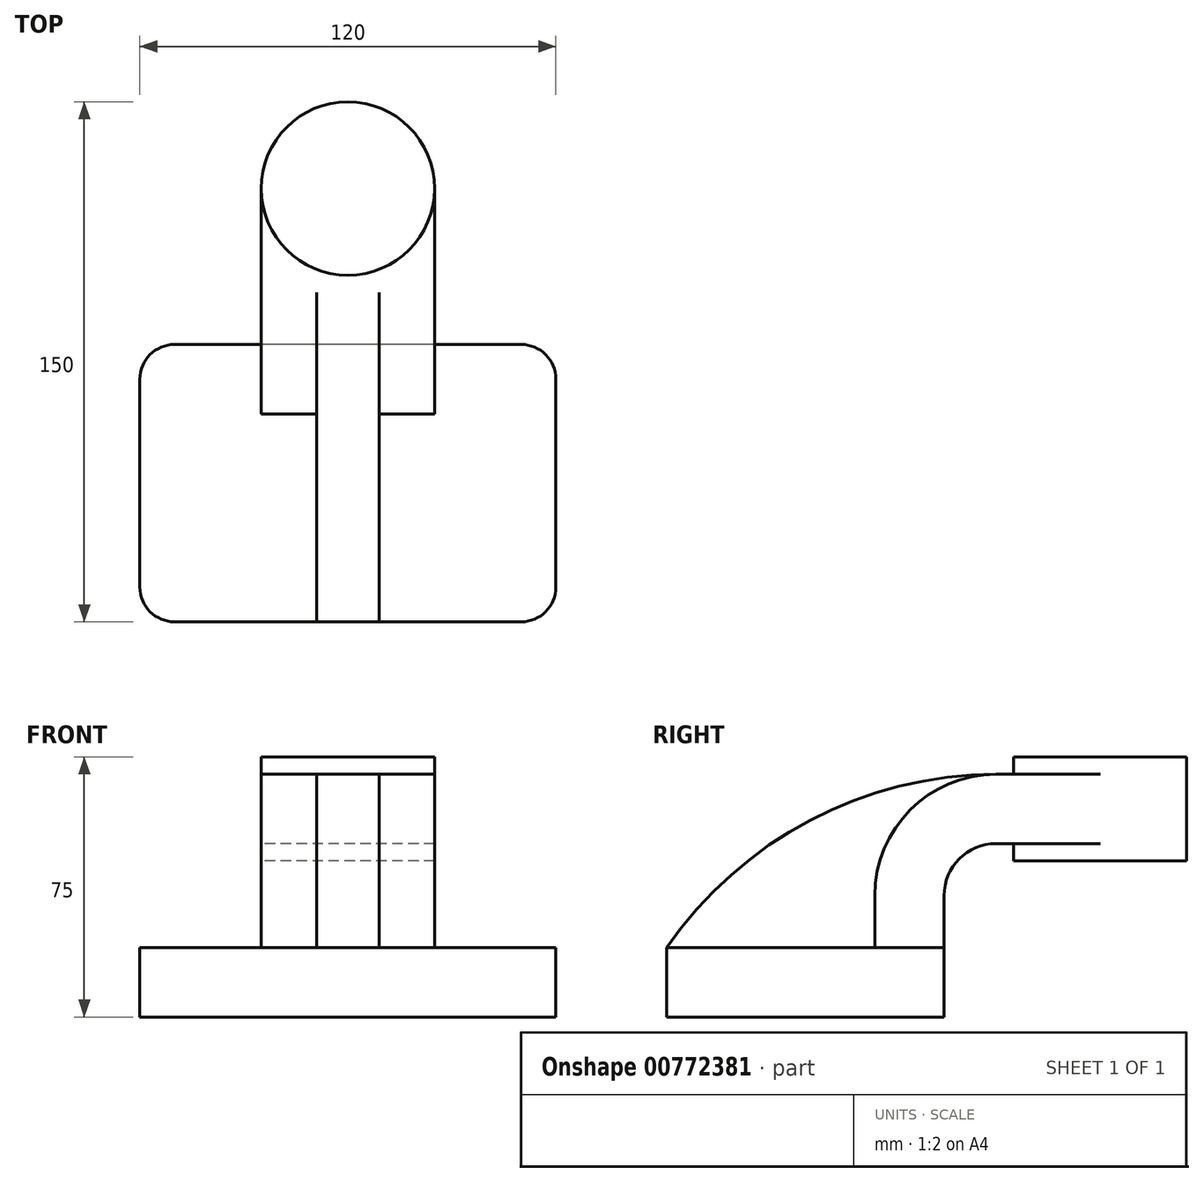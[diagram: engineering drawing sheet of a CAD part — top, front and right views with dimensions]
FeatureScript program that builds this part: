
annotation { "Feature Type Name" : "Feature", "Feature Type Description" : "" }
export const myFeature = defineFeature(function(context is Context, id is Id, definition is map)
    precondition{}
    {
        {
            var Q0;
            Q0=qCreatedBy(makeId("Right.planeOp"),FACE);
            var sketch = newSketch(context, id + "F0", { "sketchPlane" : qUnion([Q0])});
            skLineSegment(sketch, "E0", {"start": v(0, 0) * mm, "end": v(80, 0) * mm});
            skLineSegment(sketch, "E1", {"start": v(80, 0) * mm, "end": v(80, 20) * mm});
            skLineSegment(sketch, "E2", {"start": v(80, 20) * mm, "end": v(80, 35) * mm});
            skLineSegment(sketch, "E3", {"start": v(0, 0) * mm, "end": v(0, 20) * mm});
            skLineSegment(sketch, "E4", {"start": v(0, 20) * mm, "end": v(80, 20) * mm});
            skLineSegment(sketch, "E5", {"start": v(95, 70) * mm, "end": v(125, 70) * mm});
            skLineSegment(sketch, "E6", {"start": v(125, 70) * mm, "end": v(125, 50) * mm});
            skLineSegment(sketch, "E7", {"start": v(125, 50) * mm, "end": v(95, 50) * mm});
            skArc(sketch, "E8", {"start": v(80, 35) * mm, "mid": v(84.4, 45.6) * mm, "end": v(95, 50) * mm});
            skArc(sketch, "E9", {"start": v(95, 70) * mm, "mid": v(41.32, 56.74) * mm, "end": v(0, 20) * mm});
            skArc(sketch, "E10.0", {"start": v(60, 35) * mm, "mid": v(70.25, 59.75) * mm, "end": v(95, 70) * mm});
            skLineSegment(sketch, "E10.1", {"start": v(60, 20) * mm, "end": v(60, 35) * mm});
            skLineSegment(sketch, "E11.bottom", {"start": v(150, 45) * mm, "end": v(100, 45) * mm});
            skLineSegment(sketch, "E11.top", {"start": v(150, 75) * mm, "end": v(100, 75) * mm});
            skLineSegment(sketch, "E11.left", {"start": v(150, 45) * mm, "end": v(150, 75) * mm});
            skLineSegment(sketch, "E11.right", {"start": v(100, 45) * mm, "end": v(100, 75) * mm});
            skPoint(sketch, "E11.middle", {"position": v(125, 60) * mm});
            skLineSegment(sketch, "E12", {"start": v(125, 70) * mm, "end": v(125, 75) * mm});
            skLineSegment(sketch, "E13", {"start": v(125, 50) * mm, "end": v(125, 45) * mm});
            skSolve(sketch);
        }
        {
            var Q0;
            Q0=makeQuery(id+"F0.imprint","IMPRINT",FACE,{"disambiguationData":[TD([[makeQuery(id+"F0.imprint","IMPRINT",EDGE,{"derivedFrom":sQuery(id+"F0.wireOp",EDGE,"E0")}),1.0]])]});
            extrude(context, id + "F1", {"entities" : qUnion([Q0]), "endBound" : BoundingType.SYMMETRIC, "depth" : 120 * mm, "offsetDistance" : 25 * mm});
        }
        {
            var Q0;
            {var subQ0=sQuery(id+"F0.wireOp",EDGE,"E9");Q0=makeQuery(id+"F0.imprint","IMPRINT",FACE,{"disambiguationData":[TD([[makeQuery(id+"F0.imprint","IMPRINT",EDGE,{"derivedFrom":subQ0}),1.0]])]});}
            extrude(context, id + "F2", {"entities" : qUnion([Q0]), "operationType" : NewBodyOperationType.ADD, "endBound" : BoundingType.SYMMETRIC, "depth" : 18 * mm, "offsetDistance" : 25 * mm});
        }
        {
            var Q0;
            {var subQ8=sQuery(id+"F0.wireOp",EDGE,"E2");Q0=makeQuery(id+"F0.imprint","IMPRINT",FACE,{"disambiguationData":[TD([[makeQuery(id+"F0.imprint","IMPRINT",EDGE,{"derivedFrom":subQ8}),1.0]])]});}
            var Q1;
            {var subQ0=sQuery(id+"F0.wireOp",EDGE,"E6");Q1=makeQuery(id+"F0.imprint","IMPRINT",FACE,{"disambiguationData":[TD([[makeQuery(id+"F0.imprint","IMPRINT",EDGE,{"derivedFrom":subQ0}),-1.0]])]});}
            extrude(context, id + "F3", {"entities" : qUnion([Q0, Q1]), "operationType" : NewBodyOperationType.ADD, "endBound" : BoundingType.SYMMETRIC, "depth" : 50 * mm, "offsetDistance" : 25 * mm});
        }
        {
            var Q0;
            Q0=makeQuery(id+"F0.imprint","IMPRINT",FACE,{"disambiguationData":[TD([[makeQuery(id+"F0.imprint","IMPRINT",EDGE,{"derivedFrom":sQuery(id+"F0.wireOp",EDGE,"E6")}),1.0]])]});
            var Q1;
            Q1=sQuery(id+"F0.wireOp",EDGE,"E13");
            revolve(context, id + "F4", {"operationType" : NewBodyOperationType.ADD, "surfaceOperationType" : NewSurfaceOperationType.NEW, "entities" : qUnion([Q0]), "axis" : qUnion([Q1]), "revolveType" : RevolveType.FULL});
        }
        {
            var Q0;
            Q0=makeQuery(id+"F1.opExtrude","CAP_EDGE",EDGE,{"disambiguationData":[OSD([sQuery(id+"F0.wireOp",EDGE,"E3")])],"isStart":false});
            var Q1;
            Q1=makeQuery(id+"F1.opExtrude","CAP_EDGE",EDGE,{"disambiguationData":[OSD([sQuery(id+"F0.wireOp",EDGE,"E1")])],"isStart":false});
            var Q2;
            Q2=makeQuery(id+"F1.opExtrude","CAP_EDGE",EDGE,{"disambiguationData":[OSD([sQuery(id+"F0.wireOp",EDGE,"E1")])],"isStart":true});
            var Q3;
            Q3=makeQuery(id+"F1.opExtrude","CAP_EDGE",EDGE,{"disambiguationData":[OSD([sQuery(id+"F0.wireOp",EDGE,"E3")])],"isStart":true});
            fillet(context, id + "F5", {"entities" : qUnion([Q0, Q1, Q2, Q3]), "radius" : 10 * mm, "tangentPropagation" : true, "allowEdgeOverflow" : false});
        }
    });
